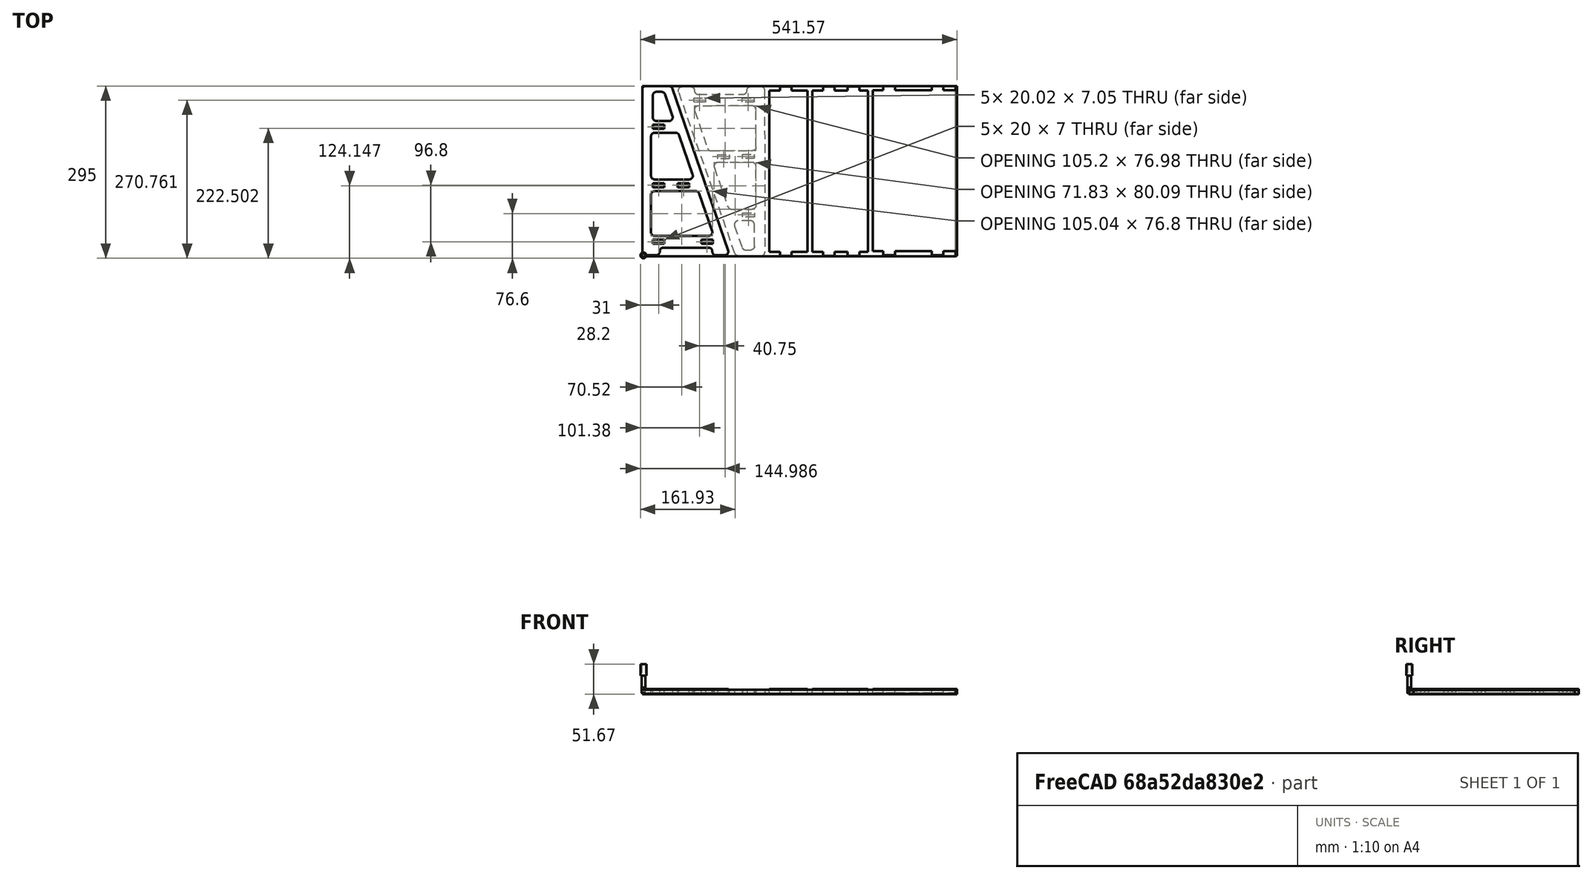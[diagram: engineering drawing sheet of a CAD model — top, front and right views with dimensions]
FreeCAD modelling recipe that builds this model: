
FCSTD DOCUMENT  (FreeCAD 0.20Rpre_28919.fc36 (Git))
Label: Stand5_DB
License: All rights reserved
LicenseURL: http://en.wikipedia.org/wiki/All_rights_reserved
objects: Part::FeaturePython×17, Path::FeaturePython×15, Sketcher::SketchObject×5, PartDesign::Body×5, PartDesign::Pad×4, App::DocumentObjectGroup×4, Mesh::FeaturePython×3, App::FeaturePython×3, App::MeasureDistance×3, Path::FeatureCompoundPython×2, PartDesign::Fillet×1, Spreadsheet::Sheet×1, Part::Mirroring×1, PartDesign::Revolution×1
note: 45 computed .brp shape members not serialized (recipe doc carries the construction recipe); baked Part::Feature solids carry a one-line shape summary decoded from their .brp

FEATURE [Sketcher::SketchObject] Sketch
  FullyConstrained = true
  MapMode = 5
  Support = -> [XY_Plane]
  expr: Constraints[101] = <<Spreadsheet>>.Thickness
  expr: Constraints[102] = <<Spreadsheet>>.TongueSize
  expr: Constraints[103] = <<Spreadsheet>>.TongueToBack
  expr: Constraints[104] = 10 - <<Spreadsheet>>.Thickness / 2
  expr: Constraints[113] = <<Spreadsheet>>.Thickness
  expr: Constraints[114] = <<Spreadsheet>>.TongueSize
  expr: Constraints[115] = <<Spreadsheet>>.TongueGapLower
  expr: Constraints[116] = 10 - <<Spreadsheet>>.Thickness / 2
  expr: Constraints[117] = 10 - <<Spreadsheet>>.Thickness / 2
  expr: Constraints[118] = 120 - <<Spreadsheet>>.Thickness / 2
  expr: Constraints[26] = <<Spreadsheet>>.Height
  expr: Constraints[27] = <<Spreadsheet>>.Top
  expr: Constraints[29] = <<Spreadsheet>>.Bottom
  expr: Constraints[55] = <<Spreadsheet>>.TongueToBack
  expr: Constraints[65] = <<Spreadsheet>>.TongueToBack
  expr: Constraints[66] = <<Spreadsheet>>.TongueSize
  expr: Constraints[67] = <<Spreadsheet>>.Thickness
  expr: Constraints[76] = 10 - <<Spreadsheet>>.Thickness / 2
  expr: Constraints[77] = <<Spreadsheet>>.TongueToBack
  expr: Constraints[78] = <<Spreadsheet>>.Thickness
  expr: Constraints[79] = <<Spreadsheet>>.TongueSize
  expr: Constraints[80] = 10 - <<Spreadsheet>>.Thickness / 2
  expr: Constraints[89] = <<Spreadsheet>>.Thickness
  expr: Constraints[90] = 10 - <<Spreadsheet>>.Thickness / 2
  expr: Constraints[91] = <<Spreadsheet>>.TongueSize
  expr: Constraints[92] = <<Spreadsheet>>.TongueGapMid
  sketch-geometry (40):
    g0: LineSegment StartX=0 StartY=290 StartZ=0 EndX=50 EndY=290 EndZ=0
    g1: LineSegment StartX=150 StartY=0 StartZ=0 EndX=120 EndY=0 EndZ=0
    g2: LineSegment StartX=0 StartY=0 StartZ=0 EndX=0 EndY=290 EndZ=0
    g3: LineSegment StartX=50 StartY=290 StartZ=0 EndX=150 EndY=0 EndZ=0
    g4: LineSegment StartX=15 StartY=210 StartZ=0 EndX=15 EndY=130 EndZ=0
    g5: LineSegment StartX=15 StartY=130 StartZ=0 EndX=89.3057 EndY=130 EndZ=0
    g6: LineSegment StartX=89.3057 StartY=130 StartZ=0 EndX=61.7195 EndY=210 EndZ=0
    g7: LineSegment StartX=61.7195 StartY=210 StartZ=0 EndX=15 EndY=210 EndZ=0
    g8: LineSegment StartX=15 StartY=110 StartZ=0 EndX=15 EndY=33.2 EndZ=0
    g9: LineSegment StartX=15 StartY=33.2 StartZ=0 EndX=122.685 EndY=33.2 EndZ=0
    g10: LineSegment StartX=122.685 StartY=33.2 StartZ=0 EndX=96.2022 EndY=110 EndZ=0
    g11: LineSegment StartX=96.2022 StartY=110 StartZ=0 EndX=15 EndY=110 EndZ=0
    g12: LineSegment StartX=120 StartY=0 StartZ=0 EndX=120 EndY=13.2 EndZ=0
    g13: LineSegment StartX=120 StartY=13.2 StartZ=0 EndX=30 EndY=13.2 EndZ=0
    g14: LineSegment StartX=30 StartY=13.2 StartZ=0 EndX=30 EndY=0 EndZ=0
    g15: LineSegment StartX=30 StartY=0 StartZ=0 EndX=0 EndY=0 EndZ=0
    g16: LineSegment StartX=18 StartY=280 StartZ=0 EndX=18 EndY=230 EndZ=0
    g17: LineSegment StartX=18 StartY=230 StartZ=0 EndX=54.8229 EndY=230 EndZ=0
    g18: LineSegment StartX=54.8229 StartY=230 StartZ=0 EndX=37.5815 EndY=280 EndZ=0
    g19: LineSegment StartX=37.5815 StartY=280 StartZ=0 EndX=18 EndY=280 EndZ=0
    g20: LineSegment StartX=18 StartY=223.5 StartZ=0 EndX=38 EndY=223.5 EndZ=0
    g21: LineSegment StartX=38 StartY=223.5 StartZ=0 EndX=38 EndY=216.5 EndZ=0
    g22: LineSegment StartX=38 StartY=216.5 StartZ=0 EndX=18 EndY=216.5 EndZ=0
    g23: LineSegment StartX=18 StartY=216.5 StartZ=0 EndX=18 EndY=223.5 EndZ=0
    g24: LineSegment StartX=18 StartY=123.5 StartZ=0 EndX=38 EndY=123.5 EndZ=0
    g25: LineSegment StartX=38 StartY=123.5 StartZ=0 EndX=38 EndY=116.5 EndZ=0
    g26: LineSegment StartX=38 StartY=116.5 StartZ=0 EndX=18 EndY=116.5 EndZ=0
    g27: LineSegment StartX=18 StartY=116.5 StartZ=0 EndX=18 EndY=123.5 EndZ=0
    g28: LineSegment StartX=60.5 StartY=123.5 StartZ=0 EndX=80.5 EndY=123.5 EndZ=0
    g29: LineSegment StartX=80.5 StartY=123.5 StartZ=0 EndX=80.5 EndY=116.5 EndZ=0
    g30: LineSegment StartX=80.5 StartY=116.5 StartZ=0 EndX=60.5 EndY=116.5 EndZ=0
    g31: LineSegment StartX=60.5 StartY=116.5 StartZ=0 EndX=60.5 EndY=123.5 EndZ=0
    g32: LineSegment StartX=18 StartY=26.7 StartZ=0 EndX=38 EndY=26.7 EndZ=0
    g33: LineSegment StartX=38 StartY=26.7 StartZ=0 EndX=38 EndY=19.7 EndZ=0
    g34: LineSegment StartX=38 StartY=19.7 StartZ=0 EndX=18 EndY=19.7 EndZ=0
    g35: LineSegment StartX=18 StartY=19.7 StartZ=0 EndX=18 EndY=26.7 EndZ=0
    g36: LineSegment StartX=101 StartY=26.7 StartZ=0 EndX=121 EndY=26.7 EndZ=0
    g37: LineSegment StartX=121 StartY=26.7 StartZ=0 EndX=121 EndY=19.7 EndZ=0
    g38: LineSegment StartX=121 StartY=19.7 StartZ=0 EndX=101 EndY=19.7 EndZ=0
    g39: LineSegment StartX=101 StartY=19.7 StartZ=0 EndX=101 EndY=26.7 EndZ=0
  constraints (119):
    c: Coincident(g15,g2)
    c: Coincident(g2,g0)
    c: Horizontal(g0)
    c: Horizontal(g1)
    c: Vertical(g2)
    c: Vertical(g4)
    c: Coincident(g4,g5)
    c: Horizontal(g5)
    c: Coincident(g5,g6)
    c: Coincident(g6,g7)
    c: Coincident(g7,g4)
    c: Vertical(g8)
    c: Coincident(g8,g9)
    c: Coincident(g9,g10)
    c: Coincident(g10,g11)
    c: Coincident(g11,g8)
    c: Horizontal(g11)
    c: Coincident(g12,g13)
    c: Coincident(g13,g14)
    c: Horizontal(g13)
    c: Vertical(g12)
    c: Vertical(g14)
    c: Coincident(g15,g-1)
    c: Coincident(g0,g3)
    c: Parallel(g3,g10)
    c: Parallel(g3,g6)
    c: DistanceY(g2,g2) = 290
    c: DistanceX(g0,g0) = 50
    c: Coincident(g3,g1)
    c: DistanceX(g2,g1) = 150
    c: DistanceX(g15,g15) = 30
    c: DistanceX(g1,g1) = 30
    c: Coincident(g12,g1)
    c: Parallel(g13,g9)
    c: Parallel(g5,g7)
    c: Coincident(g14,g15)
    c: DistanceY(g14,g13) = 13.2
    c: DistanceY(g13,g8) = 20
    c: DistanceY(g8,g4) = 20
    c: DistanceY(g4,g0) = 80
    c: DistanceX(g2,g8) = 15
    c: DistanceX(g2,g4) = 15
    c: Horizontal(g15)
    c: Distance(g5,g3) = 15
    c: Distance(g10,g3) = 15
    c: DistanceY(g1,g2) = 0
    c: Vertical(g16)
    c: Coincident(g16,g17)
    c: Horizontal(g17)
    c: Coincident(g17,g18)
    c: Coincident(g18,g19)
    c: Coincident(g19,g16)
    c: Horizontal(g19)
    c: DistanceY(g16,g0) = 10
    c: Parallel(g18,g3)
    c: DistanceX(g0,g16) = 18
    c: Distance(g17,g3) = 15
    c: Coincident(g20,g21)
    c: Coincident(g21,g22)
    c: Coincident(g22,g23)
    c: Coincident(g23,g20)
    c: Horizontal(g20)
    c: Horizontal(g22)
    c: Vertical(g21)
    c: Vertical(g23)
    c: DistanceX(g0,g20) = 18
    c: DistanceX(g20,g20) = 20
    c: DistanceY(g23,g23) = 7
    c: Coincident(g24,g25)
    c: Coincident(g25,g26)
    c: Coincident(g26,g27)
    c: Coincident(g27,g24)
    c: Horizontal(g24)
    c: Horizontal(g26)
    c: Vertical(g25)
    c: Vertical(g27)
    c: DistanceY(g20,g16) = 6.5
    c: DistanceX(g2,g26) = 18
    c: DistanceY(g27,g27) = 7
    c: DistanceX(g26,g26) = 20
    c: DistanceY(g24,g4) = 6.5
    c: Coincident(g28,g29)
    c: Coincident(g29,g30)
    c: Coincident(g30,g31)
    c: Coincident(g31,g28)
    c: Horizontal(g28)
    c: Horizontal(g30)
    c: Vertical(g29)
    c: Vertical(g31)
    c: DistanceY(g31,g31) = 7
    c: DistanceY(g28,g5) = 6.5
    c: DistanceX(g30,g30) = 20
    c: DistanceX(g24,g28) = 22.5
    c: Coincident(g32,g33)
    c: Coincident(g33,g34)
    c: Coincident(g34,g35)
    c: Coincident(g35,g32)
    c: Horizontal(g32)
    c: Horizontal(g34)
    c: Vertical(g33)
    c: Vertical(g35)
    c: DistanceY(g35,g35) = 7
    c: DistanceX(g32,g32) = 20
    c: DistanceX(g2,g34) = 18
    c: DistanceY(g32,g8) = 6.5
    c: Coincident(g36,g37)
    c: Coincident(g37,g38)
    c: Coincident(g38,g39)
    c: Coincident(g39,g36)
    c: Horizontal(g36)
    c: Horizontal(g38)
    c: Vertical(g37)
    c: Vertical(g39)
    c: DistanceY(g39,g39) = 7
    c: DistanceX(g36,g36) = 20
    c: DistanceX(g32,g36) = 63
    c: DistanceY(g36,g9) = 6.5
    c: DistanceY(g4,g22) = 6.5
    c: DistanceY(g2,g26) = 116.5
FEATURE [PartDesign::Pad] Pad
  Direction = (0,0,1)
  Length = 7
  Length2 = 100
  Profile = -> Sketch
  Type = 0
  expr: Length = <<Spreadsheet>>.Thickness
FEATURE [PartDesign::Fillet] Fillet
  Base = -> Pad [Edge20,Edge2,Edge1,Edge5,Edge8,Edge17,Edge44,Edge37,Edge32,Edge25,Edge38,Edge26,Edge29,Edge41,Edge14,Edge11,Edge49,Edge50,Edge56,Edge53]
  BaseFeature = -> Pad
  Radius = 6.5
  SupportTransform = false
  UseAllEdges = false
  expr: Radius = <<Spreadsheet>>.Tool
FEATURE [PartDesign::Body] Body
  Group = -> [Sketch,Pad,Fillet]
  Origin = -> Origin
  Placement = pos=(-2,0,0) rot=(0,0,1;0rad)
  Tip = -> Fillet
FEATURE [Spreadsheet::Sheet] Spreadsheet
  cells = A2=Material Thickness; B2(Thickness)=7; A3=Tool Size; B3(Tool)=6.5; A5=Height; B5(Height)=290; A6=Bottom Width; B6(Bottom)=150; A7=Top Width; B7(Top)=50; A8=SlotSize; B8(SlotSize)=20; A9=TongueSize; B9(TongueSize)==B8; A10=Tongue to back; B10(TongueToBack)=18; A11=Centre; B11(SlotCentre)=120; A12=Mid Tongue Gap; B12(TongueGapMid)=22.5; A13=Lower Tongue Gap; B13(TongueGapLower)=63; A15=TopShelf; B15(ShelfTop)=65; A16=MidShelf; B16(ShelfMid)==(B6 + B7) / 2 - 5; A17=Bottom Shelf; B17(ShelfBottom)==B6 - 6; A18=Shelf Width; B18(ShelfWidth)==B5 - B2 * 2
FEATURE [Part::Mirroring] mirror  label="Body (mirrored) "
  Base = (159.181,124.226,5.79083)
  Normal = (-0.999887,-0.00161748,0.0149187)
  Placement = pos=(-113.202,287.893,10.586) rot=(0.99989,0.002927,-0.014571;3.14394rad)
  Source = -> Body
FEATURE [Sketcher::SketchObject] Sketch001
  FullyConstrained = false
  MapMode = 5
  Support = -> [XY_Plane001]
  expr: Constraints[15] = <<Spreadsheet>>.TongueSize
  expr: Constraints[16] = <<Spreadsheet>>.Thickness
  expr: Constraints[24] = <<Spreadsheet>>.TongueSize
  expr: Constraints[25] = <<Spreadsheet>>.Thickness
  expr: Constraints[26] = <<Spreadsheet>>.TongueToBack
  expr: Constraints[27] = <<Spreadsheet>>.TongueToBack
  expr: Constraints[31] = <<Spreadsheet>>.ShelfWidth
  expr: Constraints[8] = <<Spreadsheet>>.ShelfTop
  expr: Constraints[9] = <<Spreadsheet>>.ShelfWidth
  sketch-geometry (12):
    g0: LineSegment StartX=222.605 StartY=283 StartZ=0 EndX=240.605 EndY=283 EndZ=0
    g1: LineSegment StartX=287.605 StartY=283 StartZ=0 EndX=287.605 EndY=7 EndZ=0
    g2: LineSegment StartX=287.605 StartY=7 StartZ=0 EndX=260.605 EndY=7 EndZ=0
    g3: LineSegment StartX=222.605 StartY=7 StartZ=0 EndX=222.605 EndY=283 EndZ=0
    g4: LineSegment StartX=260.605 StartY=7 StartZ=0 EndX=260.605 EndY=0 EndZ=0
    g5: LineSegment StartX=260.605 StartY=0 StartZ=0 EndX=240.605 EndY=0 EndZ=0
    g6: LineSegment StartX=240.605 StartY=0 StartZ=0 EndX=240.605 EndY=7 EndZ=0
    g7: LineSegment StartX=240.605 StartY=7 StartZ=0 EndX=222.605 EndY=7 EndZ=0
    g8: LineSegment StartX=240.605 StartY=290 StartZ=0 EndX=260.605 EndY=290 EndZ=0
    g9: LineSegment StartX=260.605 StartY=290 StartZ=0 EndX=260.605 EndY=283 EndZ=0
    g10: LineSegment StartX=240.605 StartY=283 StartZ=0 EndX=240.605 EndY=290 EndZ=0
    g11: LineSegment StartX=260.605 StartY=283 StartZ=0 EndX=287.605 EndY=283 EndZ=0
  constraints (35):
    c: Coincident(g11,g1)
    c: Coincident(g1,g2)
    c: Coincident(g7,g3)
    c: Coincident(g3,g0)
    c: Horizontal(g0)
    c: Horizontal(g2)
    c: Vertical(g1)
    c: Vertical(g3)
    c: DistanceX(g0,g11) = 65
    c: DistanceY(g3,g3) = 276
    c: Coincident(g4,g5)
    c: Coincident(g5,g6)
    c: Horizontal(g5)
    c: Vertical(g4)
    c: Vertical(g6)
    c: DistanceX(g5,g5) = 20
    c: DistanceY(g4,g4) = 7
    c: DistanceY(g-1,g5) = 0
    c: Parallel(g5,g7)
    c: Coincident(g8,g9)
    c: Coincident(g10,g8)
    c: Horizontal(g8)
    c: Vertical(g9)
    c: Vertical(g10)
    c: DistanceX(g8,g8) = 20
    c: DistanceY(g9,g9) = 7
    c: DistanceX(g0,g8) = 18
    c: DistanceX(g3,g5) = 18
    c: Coincident(g7,g6)
    c: Coincident(g11,g9)
    c: Coincident(g2,g4)
    c: DistanceY(g1,g1) = 276
    c: Parallel(g11,g8)
    c: Equal(g4,g6)
    c: Coincident(g0,g10)
FEATURE [PartDesign::Pad] Pad001
  Direction = (0,0,1)
  Length = 7
  Length2 = 10
  Profile = -> Sketch001
  Type = 0
  expr: Length = <<Spreadsheet>>.Thickness
FEATURE [PartDesign::Body] Body001  label="TopShelf"
  Group = -> [Sketch001,Pad001]
  Origin = -> Origin001
  Placement = pos=(-7,-1,0) rot=(0,0,1;0rad)
  Tip = -> Pad001
FEATURE [Sketcher::SketchObject] Sketch002
  FullyConstrained = false
  MapMode = 5
  Support = -> [XY_Plane002]
  expr: Constraints[31] = <<Spreadsheet>>.TongueToBack
  expr: Constraints[32] = <<Spreadsheet>>.TongueGapMid
  expr: Constraints[33] = <<Spreadsheet>>.TongueSize
  expr: Constraints[36] = <<Spreadsheet>>.TongueSize
  expr: Constraints[37] = <<Spreadsheet>>.TongueToBack
  expr: Constraints[38] = <<Spreadsheet>>.TongueSize
  expr: Constraints[42] = <<Spreadsheet>>.TongueGapMid
  expr: Constraints[43] = <<Spreadsheet>>.TongueSize
  expr: Constraints[46] = <<Spreadsheet>>.Thickness
  expr: Constraints[47] = <<Spreadsheet>>.Thickness
  expr: Constraints[48] = <<Spreadsheet>>.Thickness
  expr: Constraints[49] = <<Spreadsheet>>.Thickness
  expr: Constraints[54] = <<Spreadsheet>>.Thickness
  expr: Constraints[55] = <<Spreadsheet>>.Thickness
  expr: Constraints[56] = <<Spreadsheet>>.Thickness
  expr: Constraints[57] = <<Spreadsheet>>.ShelfWidth
  expr: Constraints[58] = <<Spreadsheet>>.Thickness
  expr: Constraints[8] = <<Spreadsheet>>.ShelfWidth
  expr: Constraints[9] = <<Spreadsheet>>.ShelfMid
  sketch-geometry (20):
    g0: LineSegment StartX=282.276 StartY=276 StartZ=0 EndX=300.276 EndY=276 EndZ=0
    g1: LineSegment StartX=377.276 StartY=276 StartZ=0 EndX=377.276 EndY=0 EndZ=0
    g2: LineSegment StartX=377.276 StartY=0 StartZ=0 EndX=362.776 EndY=0 EndZ=0
    g3: LineSegment StartX=282.276 StartY=0 StartZ=0 EndX=282.276 EndY=276 EndZ=0
    g4: LineSegment StartX=300.276 StartY=283 StartZ=0 EndX=320.276 EndY=283 EndZ=0
    g5: LineSegment StartX=320.276 StartY=283 StartZ=0 EndX=320.276 EndY=276 EndZ=0
    g6: LineSegment StartX=300.276 StartY=276 StartZ=0 EndX=300.276 EndY=283 EndZ=0
    g7: LineSegment StartX=342.776 StartY=283 StartZ=0 EndX=362.776 EndY=283 EndZ=0
    g8: LineSegment StartX=362.776 StartY=283 StartZ=0 EndX=362.776 EndY=276 EndZ=0
    g9: LineSegment StartX=342.776 StartY=276 StartZ=0 EndX=342.776 EndY=283 EndZ=0
    g10: LineSegment StartX=320.276 StartY=-2e-16 StartZ=0 EndX=320.276 EndY=-7 EndZ=0
    g11: LineSegment StartX=320.276 StartY=-7 StartZ=0 EndX=300.276 EndY=-7 EndZ=0
    g12: LineSegment StartX=300.276 StartY=-7 StartZ=0 EndX=300.276 EndY=0 EndZ=0
    g13: LineSegment StartX=362.776 StartY=0 StartZ=0 EndX=362.776 EndY=-7 EndZ=0
    g14: LineSegment StartX=362.776 StartY=-7 StartZ=0 EndX=342.776 EndY=-7 EndZ=0
    g15: LineSegment StartX=342.776 StartY=-7 StartZ=0 EndX=342.776 EndY=0 EndZ=0
    g16: LineSegment StartX=320.276 StartY=276 StartZ=0 EndX=342.776 EndY=276 EndZ=0
    g17: LineSegment StartX=362.776 StartY=276 StartZ=0 EndX=377.276 EndY=276 EndZ=0
    g18: LineSegment StartX=300.276 StartY=0 StartZ=0 EndX=282.276 EndY=0 EndZ=0
    g19: LineSegment StartX=342.776 StartY=0 StartZ=0 EndX=320.276 EndY=-2e-16 EndZ=0
  constraints (60):
    c: Coincident(g17,g1)
    c: Coincident(g1,g2)
    c: Coincident(g18,g3)
    c: Coincident(g3,g0)
    c: Horizontal(g0)
    c: Horizontal(g2)
    c: Vertical(g1)
    c: Vertical(g3)
    c: DistanceY(g1,g1) = 276
    c: DistanceX(g0,g17) = 95
    c: Coincident(g4,g5)
    c: Coincident(g6,g4)
    c: Horizontal(g4)
    c: Vertical(g5)
    c: Vertical(g6)
    c: Coincident(g7,g8)
    c: Coincident(g9,g7)
    c: Horizontal(g7)
    c: Vertical(g8)
    c: Vertical(g9)
    c: PointOnObject(g8,g0)
    c: Coincident(g10,g11)
    c: Coincident(g11,g12)
    c: Horizontal(g11)
    c: Vertical(g10)
    c: Vertical(g12)
    c: Coincident(g13,g14)
    c: Coincident(g14,g15)
    c: Horizontal(g14)
    c: Vertical(g13)
    c: Vertical(g15)
    c: DistanceX(g0,g4) = 18
    c: DistanceX(g4,g7) = 22.5
    c: DistanceX(g4,g4) = 20
    c: Coincident(g16,g5)
    c: PointOnObject(g16,g9)
    c: DistanceX(g7,g7) = 20
    c: DistanceX(g3,g11) = 18
    c: DistanceX(g11,g11) = 20
    c: Coincident(g18,g12)
    c: Coincident(g10,g19)
    c: Coincident(g19,g15)
    c: DistanceX(g19,g19) = 22.5
    c: DistanceX(g14,g14) = 20
    c: Coincident(g0,g6)
    c: Coincident(g17,g8)
    c: DistanceY(g1,g7) = 7
    c: DistanceY(g9,g9) = 7
    c: DistanceY(g5,g5) = 7
    c: DistanceY(g6,g6) = 7
    c: Parallel(g16,g4)
    c: Parallel(g18,g11)
    c: Parallel(g19,g11)
    c: Coincident(g2,g13)
    c: DistanceY(g12,g12) = 7
    c: DistanceY(g15,g15) = 7
    c: DistanceY(g13,g13) = 7
    c: DistanceY(g3,g3) = 276
    c: DistanceY(g10,g10) = 7
    c: PointOnObject(g3,g-1)
FEATURE [PartDesign::Pad] Pad002
  Direction = (0,0,1)
  Length = 7
  Length2 = 10
  Profile = -> Sketch002
  Type = 0
  expr: Length = <<Spreadsheet>>.Thickness
FEATURE [PartDesign::Body] Body002  label="MidShelf"
  Group = -> [Sketch002,Pad002]
  Origin = -> Origin002
  Placement = pos=(7,6,0) rot=(0,0,1;0rad)
  Tip = -> Pad002
FEATURE [Sketcher::SketchObject] Sketch003
  FullyConstrained = false
  MapMode = 5
  Support = -> [XY_Plane003]
  expr: Constraints[34] = <<Spreadsheet>>.TongueSize
  expr: Constraints[35] = <<Spreadsheet>>.TongueSize
  expr: Constraints[36] = <<Spreadsheet>>.TongueGapLower
  expr: Constraints[37] = <<Spreadsheet>>.TongueToBack
  expr: Constraints[44] = <<Spreadsheet>>.Thickness
  expr: Constraints[45] = <<Spreadsheet>>.Thickness
  expr: Constraints[46] = <<Spreadsheet>>.Thickness
  expr: Constraints[48] = <<Spreadsheet>>.ShelfWidth
  expr: Constraints[49] = <<Spreadsheet>>.Thickness
  expr: Constraints[4] = <<Spreadsheet>>.ShelfBottom
  expr: Constraints[50] = <<Spreadsheet>>.Thickness
  expr: Constraints[51] = <<Spreadsheet>>.TongueSize
  expr: Constraints[52] = <<Spreadsheet>>.TongueSize
  expr: Constraints[53] = <<Spreadsheet>>.TongueGapLower
  expr: Constraints[54] = <<Spreadsheet>>.TongueToBack
  expr: Constraints[55] = <<Spreadsheet>>.ShelfWidth
  expr: Constraints[56] = <<Spreadsheet>>.Thickness
  expr: Constraints[57] = <<Spreadsheet>>.Thickness
  expr: Constraints[58] = 11mm
  sketch-geometry (20):
    g0: LineSegment StartX=535.567 StartY=287 StartZ=0 EndX=535.567 EndY=11 EndZ=0
    g1: LineSegment StartX=535.567 StartY=11 StartZ=0 EndX=512.567 EndY=11 EndZ=0
    g2: LineSegment StartX=391.567 StartY=11 StartZ=0 EndX=391.567 EndY=287 EndZ=0
    g3: LineSegment StartX=409.567 StartY=294 StartZ=0 EndX=429.567 EndY=294 EndZ=0
    g4: LineSegment StartX=429.567 StartY=294 StartZ=0 EndX=429.567 EndY=287 EndZ=0
    g5: LineSegment StartX=409.567 StartY=287 StartZ=0 EndX=409.567 EndY=294 EndZ=0
    g6: LineSegment StartX=492.567 StartY=294 StartZ=0 EndX=512.567 EndY=294 EndZ=0
    g7: LineSegment StartX=512.567 StartY=294 StartZ=0 EndX=512.567 EndY=287 EndZ=0
    g8: LineSegment StartX=492.567 StartY=287 StartZ=0 EndX=492.567 EndY=294 EndZ=0
    g9: LineSegment StartX=429.567 StartY=11 StartZ=0 EndX=429.567 EndY=4 EndZ=0
    g10: LineSegment StartX=429.567 StartY=4 StartZ=0 EndX=409.567 EndY=4 EndZ=0
    g11: LineSegment StartX=409.567 StartY=4 StartZ=0 EndX=409.567 EndY=11 EndZ=0
    g12: LineSegment StartX=512.567 StartY=11 StartZ=0 EndX=512.567 EndY=4 EndZ=0
    g13: LineSegment StartX=512.567 StartY=4 StartZ=0 EndX=492.567 EndY=4 EndZ=0
    g14: LineSegment StartX=492.567 StartY=4 StartZ=0 EndX=492.567 EndY=11 EndZ=0
    g15: LineSegment StartX=391.567 StartY=287 StartZ=0 EndX=409.567 EndY=287 EndZ=0
    g16: LineSegment StartX=429.567 StartY=287 StartZ=0 EndX=492.567 EndY=287 EndZ=0
    g17: LineSegment StartX=512.567 StartY=287 StartZ=0 EndX=535.567 EndY=287 EndZ=0
    g18: LineSegment StartX=409.567 StartY=11 StartZ=0 EndX=391.567 EndY=11 EndZ=0
    g19: LineSegment StartX=492.567 StartY=11 StartZ=0 EndX=429.567 EndY=11 EndZ=0
  constraints (59):
    c: Coincident(g0,g1)
    c: Coincident(g18,g2)
    c: Horizontal(g1)
    c: Vertical(g0)
    c: DistanceX(g2,g0) = 144
    c: Coincident(g3,g4)
    c: Coincident(g5,g3)
    c: Horizontal(g3)
    c: Vertical(g4)
    c: Vertical(g5)
    c: Coincident(g6,g7)
    c: Coincident(g8,g6)
    c: Horizontal(g6)
    c: Vertical(g7)
    c: Vertical(g8)
    c: Coincident(g9,g10)
    c: Coincident(g10,g11)
    c: Horizontal(g10)
    c: Vertical(g9)
    c: Vertical(g11)
    c: Coincident(g12,g13)
    c: Coincident(g13,g14)
    c: Horizontal(g13)
    c: Vertical(g12)
    c: Vertical(g14)
    c: Horizontal(g17)
    c: Coincident(g7,g17)
    c: Coincident(g17,g0)
    c: Coincident(g8,g16)
    c: Coincident(g16,g4)
    c: Coincident(g15,g5)
    c: Coincident(g2,g15)
    c: Parallel(g15,g3)
    c: Parallel(g16,g3)
    c: DistanceX(g3,g3) = 20
    c: DistanceX(g6,g6) = 20
    c: DistanceX(g3,g6) = 63
    c: DistanceX(g2,g3) = 18
    c: Coincident(g18,g11)
    c: Coincident(g9,g19)
    c: Coincident(g19,g14)
    c: Coincident(g12,g1)
    c: Parallel(g18,g10)
    c: Parallel(g10,g19)
    c: DistanceY(g11,g11) = 7
    c: DistanceY(g9,g9) = 7
    c: DistanceY(g14,g14) = 7
    c: Perpendicular(g18,g2)
    c: DistanceY(g2,g2) = 276
    c: DistanceY(g5,g5) = 7
    c: DistanceY(g8,g8) = 7
    c: DistanceX(g10,g10) = 20
    c: DistanceX(g13,g13) = 20
    c: DistanceX(g19,g19) = 63
    c: DistanceX(g18,g18) = 18
    c: DistanceY(g0,g0) = 276
    c: DistanceY(g12,g12) = 7
    c: DistanceY(g7,g7) = 7
    c: DistanceY(g-1,g2) = 11
FEATURE [PartDesign::Pad] Pad003
  Direction = (0,0,1)
  Length = 7
  Length2 = 10
  Profile = -> Sketch003
  Type = 0
  expr: Length = <<Spreadsheet>>.Thickness
FEATURE [PartDesign::Body] Body003  label="BottomShelf"
  Group = -> [Sketch003,Pad003]
  Origin = -> Origin003
  Placement = pos=(1,-4,0) rot=(0,0,1;0rad)
  Tip = -> Pad003
FEATURE [Mesh::FeaturePython] CutMaterial001  # WARN: FeaturePython — macro-defined, semantics opaque (R4)
FEATURE [App::FeaturePython] SetupSheet  # Path/CAM operation (typed FeaturePython)
  ClearanceHeightExpression = OpStockZMax+SetupSheet.ClearanceHeightOffset
  ClearanceHeightOffset = 5
  CoolantMode = 0
  CoolantModes = None | Flood | Mist
  FinalDepthExpression = OpFinalDepth
  HorizRapid = 0
  SafeHeightExpression = OpStockZMax+SetupSheet.SafeHeightOffset
  SafeHeightOffset = 3
  StartDepthExpression = OpStartDepth
  StepDownExpression = OpToolDiameter
  VertRapid = 0
FEATURE [Part::FeaturePython] Clone  label="Model-Body"  # Draft clone (typed FeaturePython)
  AttacherType = Attacher::AttachEngine3D
  Fuse = false
  Objects = -> [Body]
  PathResource = Model
  Placement = pos=(-2,0,0) rot=(0,0,1;0rad)
  Scale = (1,1,1)
FEATURE [Part::FeaturePython] Clone001  label="Model-Body (mirrored) "  # Draft clone (typed FeaturePython)
  AttacherType = Attacher::AttachEngine3D
  Fuse = false
  Objects = -> [mirror]
  PathResource = Model
  Placement = pos=(-113.202,287.893,10.586) rot=(0.99989,0.002927,-0.014571;3.14394rad)
  Scale = (1,1,1)
FEATURE [Part::FeaturePython] Clone002  label="Model-BottomShelf"  # Draft clone (typed FeaturePython)
  AttacherType = Attacher::AttachEngine3D
  Fuse = false
  Objects = -> [Body003]
  PathResource = Model
  Placement = pos=(1,-4,0) rot=(0,0,1;0rad)
  Scale = (1,1,1)
FEATURE [Part::FeaturePython] Clone003  label="Model-MidShelf"  # Draft clone (typed FeaturePython)
  AttacherType = Attacher::AttachEngine3D
  Fuse = false
  Objects = -> [Body002]
  PathResource = Model
  Placement = pos=(7,6,0) rot=(0,0,1;0rad)
  Scale = (1,1,1)
FEATURE [Part::FeaturePython] Clone004  label="Model-TopShelf"  # Draft clone (typed FeaturePython)
  AttacherType = Attacher::AttachEngine3D
  Fuse = false
  Objects = -> [Body001]
  PathResource = Model
  Placement = pos=(-7,-1,0) rot=(0,0,1;0rad)
  Scale = (1,1,1)
FEATURE [App::DocumentObjectGroup] Model
  Group = -> [Clone,Clone001,Clone002,Clone003,Clone004,SetupSheet]
FEATURE [Part::FeaturePython] Stock001  # WARN: FeaturePython — macro-defined, semantics opaque (R4)
  Height = 7.17
  Length = 536.13
  Placement = pos=(-2,-1.61323,-0.917831) rot=(0,0,1;0rad)
  StockType = CreateBox
  Width = 291.61
FEATURE [Part::FeaturePython] ToolBit001  label="6.4mm Endmill"  # Path/CAM toolbit (typed FeaturePython)
  BitPropertyNames = Chipload | CuttingEdgeHeight | Diameter | Flutes | Length | Material | ShankDiameter
  BitShape = <path>
  Chipload = 0
  CuttingEdgeHeight = 30
  Diameter = 6.4
  File = <userpath>/MensShed/CNCRouter/FreeCAD/Bit/6.4mm_Endmill.fctb
  Flutes = 0
  Length = 50
  Material = 0
  ShankDiameter = 10
  ShapeName = endmill
FEATURE [Sketcher::SketchObject] Sketch004
  FullyConstrained = true
  MapMode = 5
  Placement = pos=(0,0,0) rot=(1,0,0;1.5708rad)
  Support = -> [XZ_Plane004]
  expr: Constraints[10] = <<Attributes>>.Length
  expr: Constraints[16] = <<Attributes>>.ShankDiameter
  expr: Constraints[18] = <<Attributes>>.CuttingEdgeHeight
  expr: Constraints[9] = <<Attributes>>.Diameter
  sketch-geometry (8):
    g0: LineSegment StartX=0 StartY=50 StartZ=0 EndX=0 EndY=0 EndZ=0
    g1: LineSegment StartX=0 StartY=0 StartZ=0 EndX=3.2 EndY=0 EndZ=0
    g2: LineSegment StartX=3.2 StartY=0 StartZ=0 EndX=3.2 EndY=30 EndZ=0
    g3: LineSegment StartX=5 StartY=50 StartZ=0 EndX=0 EndY=50 EndZ=0
    g4: LineSegment StartX=3.2 StartY=0 StartZ=0 EndX=-3.2 EndY=0 EndZ=0
    g5: LineSegment StartX=5 StartY=29.99 StartZ=0 EndX=3.2 EndY=30 EndZ=0
    g6: LineSegment StartX=5 StartY=50 StartZ=0 EndX=5 EndY=29.99 EndZ=0
    g7: LineSegment StartX=-5 StartY=50 StartZ=0 EndX=5 EndY=50 EndZ=0
  constraints (21):
    c: Vertical(g0)
    c: Coincident(g0,g1)
    c: Horizontal(g1)
    c: Coincident(g1,g2)
    c: Vertical(g2)
    c: Horizontal(g3)
    c: Coincident(g0,g3)
    c: Coincident(g4,g1)
    c: Symmetric(g1,g4,g0)
    c: DistanceX(g4,g4) = 6.4
    c: DistanceY(g2,g3) = 50
    c: Coincident(g2,g5)
    c: Vertical(g6)
    c: Coincident(g3,g6)
    c: Symmetric(g7,g7,g0)
    c: Coincident(g7,g3)
    c: DistanceX(g7,g7) = 10
    c: Coincident(g5,g6)
    c: DistanceY(g2) = 30
    c: Coincident(g0,g-1)
    c: DistanceY(g5,g2) = 0.01
FEATURE [PartDesign::Revolution] Revolution
  AllowMultiFace = false
  Angle = 360
  Axis = (0,-2e-16,1)
  Base = (0,0,0)
  Placement = pos=(0,0,0) rot=(1,0,0;1.5708rad)
  Profile = -> Sketch004
  ReferenceAxis = -> Sketch004 [V_Axis]
  Reversed = true
FEATURE [App::FeaturePython] PropertyBag  label="Attributes"  # WARN: FeaturePython — macro-defined, semantics opaque (R4)
  Chipload = 0
  CustomPropertyGroups = Attributes | Shape
  CuttingEdgeHeight = 30
  Diameter = 6.4
  Flutes = 0
  Length = 50
  Material = 0
  ShankDiameter = 10
FEATURE [PartDesign::Body] Body004  label="Endmill001"
  Group = -> [Sketch004,Revolution,PropertyBag]
  Origin = -> Origin004
  Tip = -> Revolution
FEATURE [Part::FeaturePython] ToolBit  label="6.4mm Endmill002"  # Path/CAM toolbit (typed FeaturePython)
  BitBody = -> Body004
  BitPropertyNames = Chipload | CuttingEdgeHeight | Diameter | Flutes | Length | Material | ShankDiameter
  BitShape = <path>
  Chipload = 0
  CuttingEdgeHeight = 30
  Diameter = 6.4
  Flutes = 0
  Length = 50
  Material = 0
  ShankDiameter = 10
  ShapeName = endmill
FEATURE [Part::FeaturePython] ToolBit002  label="6.4mm Endmill003"  # Path/CAM toolbit (typed FeaturePython)
  BitPropertyNames = Chipload | CuttingEdgeHeight | Diameter | Flutes | Length | Material | ShankDiameter
  BitShape = <path>
  Chipload = 0
  CuttingEdgeHeight = 30
  Diameter = 6.4
  Flutes = 0
  Length = 50
  Material = 0
  ShankDiameter = 10
  ShapeName = endmill
FEATURE [Path::FeaturePython] __4mm_Endmill  label="6.4mm Endmill001"  # Path/CAM operation (typed FeaturePython)
  HorizFeed = 13.5167
  HorizRapid = 0
  SpindleDir = 1
  SpindleSpeed = 12682
  Tool = -> ToolBit002
  ToolNumber = 2
  VertFeed = 6.75
  VertRapid = 0
  expr: VertRapid = SetupSheet.VertRapid
FEATURE [Path::FeaturePython] Profile  label="BaseInner"  # Path/CAM operation (typed FeaturePython)
  Active = true
  AreaParams:
    Tolerance = 1e-07
    FitArcs = True
    Simplify = False
    CleanDistance = 0.0
    Accuracy = 0.01
    Unit = 1.0
    MinArcPoints = 4
    MaxArcPoints = 100
    ClipperScale = 10000000.0
    Fill = 0
    Coplanar = 0
    Reorient = True
    Outline = False
    Explode = False
    OpenMode = 0
    Deflection = 0.01
    SubjectFill = 0
    ClipFill = 0
    Offset = -3.2
    ExtraPass = 0
    Stepover = 0.0
    LastStepover = 0.0
    JoinType = 0
    EndType = 0
    MiterLimit = 2.0
    RoundPrecision = 0.0
    PocketMode = 0
    ToolRadius = 1.0
    PocketExtraOffset = 0.0
    PocketStepover = 0.0
    PocketLastStepover = 0.0
    FromCenter = False
    Angle = 45.0
    AngleShift = 0.0
    Shift = 0.0
    Thicken = False
    SectionCount = -1
    Stepdown = 1.0
    SectionOffset = 0.0
    SectionTolerance = 1e-06
    SectionMode = 2
    Project = False
  AttemptInverseAngle = true
  Base = -> [Clone]
  ClearanceHeight = 11.2522
  CoolantMode = 0
  CycleTime = 00:03:00
  Direction = 0
  EnableRotation = 0
  FinalDepth = 0.2
  HandleMultipleFeatures = 0
  InverseAngle = false
  JoinType = 0
  LimitDepthToFace = true
  MiterLimit = 0.1
  OffsetExtra = 0
  OpFinalDepth = 7
  OpStartDepth = 10
  OpStockZMax = 6.25217
  OpStockZMin = -0.917831
  OpToolDiameter = 6.4
  PathParams = {'orientation': 1, 'feedrate': 13.516666666666666, 'feedrate_v': 6.75, 'verbose': True, 'resume_height': 9.252168804445907, 'retraction': 11.252168804445907, 'return_end': True, 'preamble': False, 'start': Vector (79.51085861020287, 133.4790016587114, 11.252168804445907)}
  ReverseDirection = false
  SafeHeight = 9.25217
  Side = 1
  SplitArcs = false
  StartDepth = 7
  StartPoint = (0,0,0)
  StepDown = 3
  ToolController = -> __4mm_Endmill
  UseComp = true
  UseStartPoint = false
  processCircles = false
  processHoles = false
  processPerimeter = true
  expr: ClearanceHeight = OpStockZMax + SetupSheet.ClearanceHeightOffset
  expr: FinalDepth = 0.2
  expr: SafeHeight = OpStockZMax + SetupSheet.SafeHeightOffset
  expr: StartDepth = <<Spreadsheet>>.Thickness
  expr: StepDown = 3
FEATURE [Path::FeaturePython] Profile001  label="MirrorInner"  # Path/CAM operation (typed FeaturePython)
  Active = true
  AreaParams:
    Tolerance = 1e-07
    FitArcs = True
    Simplify = False
    CleanDistance = 0.0
    Accuracy = 0.01
    Unit = 1.0
    MinArcPoints = 4
    MaxArcPoints = 100
    ClipperScale = 10000000.0
    Fill = 0
    Coplanar = 0
    Reorient = True
    Outline = False
    Explode = False
    OpenMode = 0
    Deflection = 0.01
    SubjectFill = 0
    ClipFill = 0
    Offset = -3.2
    ExtraPass = 0
    Stepover = 0.0
    LastStepover = 0.0
    JoinType = 0
    EndType = 0
    MiterLimit = 2.0
    RoundPrecision = 0.0
    PocketMode = 0
    ToolRadius = 1.0
    PocketExtraOffset = 0.0
    PocketStepover = 0.0
    PocketLastStepover = 0.0
    FromCenter = False
    Angle = 45.0
    AngleShift = 0.0
    Shift = 0.0
    Thicken = False
    SectionCount = -1
    Stepdown = 1.0
    SectionOffset = 0.0
    SectionTolerance = 1e-06
    SectionMode = 2
    Project = False
  AttemptInverseAngle = true
  Base = -> [Clone001]
  ClearanceHeight = 11.2522
  CoolantMode = 0
  CycleTime = 00:03:02
  Direction = 0
  EnableRotation = 0
  FinalDepth = 0.2
  HandleMultipleFeatures = 0
  InverseAngle = false
  JoinType = 0
  LimitDepthToFace = true
  MiterLimit = 0.1
  OffsetExtra = 0
  OpFinalDepth = 5.95233
  OpStartDepth = 6.25217
  OpStockZMax = 6.25217
  OpStockZMin = -0.917831
  OpToolDiameter = 6.4
  PathParams = {'orientation': 1, 'feedrate': 13.516666666666666, 'feedrate_v': 6.75, 'verbose': True, 'resume_height': 9.252168804445907, 'retraction': 11.252168804445907, 'return_end': True, 'preamble': False, 'start': Vector (185.594594529693, 82.4083677149265, 11.252168804445907)}
  ReverseDirection = false
  SafeHeight = 9.25217
  Side = 1
  SplitArcs = false
  StartDepth = 7
  StartPoint = (0,0,0)
  StepDown = 3
  ToolController = -> __4mm_Endmill
  UseComp = true
  UseStartPoint = false
  processCircles = false
  processHoles = false
  processPerimeter = true
  expr: ClearanceHeight = OpStockZMax + SetupSheet.ClearanceHeightOffset
  expr: FinalDepth = 0.2
  expr: SafeHeight = OpStockZMax + SetupSheet.SafeHeightOffset
  expr: StartDepth = <<Spreadsheet>>.Thickness
  expr: StepDown = 3
FEATURE [Path::FeaturePython] Profile002  label="Outer Profile"  # Path/CAM operation (typed FeaturePython)
  Active = true
  AreaParams:
    Tolerance = 1e-07
    FitArcs = True
    Simplify = False
    CleanDistance = 0.0
    Accuracy = 0.01
    Unit = 1.0
    MinArcPoints = 4
    MaxArcPoints = 100
    ClipperScale = 10000000.0
    Fill = 0
    Coplanar = 0
    Reorient = True
    Outline = False
    Explode = False
    OpenMode = 0
    Deflection = 0.01
    SubjectFill = 0
    ClipFill = 0
    Offset = 3.2
    ExtraPass = 0
    Stepover = 0.0
    LastStepover = 0.0
    JoinType = 0
    EndType = 0
    MiterLimit = 2.0
    RoundPrecision = 0.0
    PocketMode = 0
    ToolRadius = 1.0
    PocketExtraOffset = 0.0
    PocketStepover = 0.0
    PocketLastStepover = 0.0
    FromCenter = False
    Angle = 45.0
    AngleShift = 0.0
    Shift = 0.0
    Thicken = False
    SectionCount = -1
    Stepdown = 1.0
    SectionOffset = 0.0
    SectionTolerance = 1e-06
    SectionMode = 2
    Project = False
  AttemptInverseAngle = true
  ClearanceHeight = 11.2522
  CoolantMode = 0
  CycleTime = 00:15:35
  Direction = 0
  EnableRotation = 0
  FinalDepth = 0.2
  HandleMultipleFeatures = 0
  InverseAngle = false
  JoinType = 0
  LimitDepthToFace = true
  MiterLimit = 0.1
  OffsetExtra = 0
  OpFinalDepth = -0.917831
  OpStartDepth = 6.25217
  OpStockZMax = 6.25217
  OpStockZMin = -0.917831
  OpToolDiameter = 6.4
  PathParams = {'orientation': 1, 'feedrate': 13.516666666666666, 'feedrate_v': 6.75, 'verbose': True, 'resume_height': 9.252168804445907, 'retraction': 11.252168804445907, 'return_end': True, 'preamble': False, 'start': Vector (286.075665, 263.59583288242766, 11.252168804445907)}
  ReverseDirection = false
  SafeHeight = 9.25217
  Side = 0
  SplitArcs = false
  StartDepth = 7
  StartPoint = (0,0,0)
  StepDown = 3
  ToolController = -> __4mm_Endmill
  UseComp = true
  UseStartPoint = false
  processCircles = false
  processHoles = false
  processPerimeter = true
  expr: ClearanceHeight = OpStockZMax + SetupSheet.ClearanceHeightOffset
  expr: FinalDepth = 0.2
  expr: SafeHeight = OpStockZMax + SetupSheet.SafeHeightOffset
  expr: StartDepth = <<Spreadsheet>>.Thickness
  expr: StepDown = 3
FEATURE [Part::FeaturePython] ToolBit003  label="3mm_Endmill"  # Path/CAM toolbit (typed FeaturePython)
  BitPropertyNames = Chipload | CuttingEdgeHeight | Diameter | Flutes | Length | Material | ShankDiameter
  BitShape = <path>
  Chipload = 0
  CuttingEdgeHeight = 10
  Diameter = 3
  File = <userpath>/MensShed/CNCRouter/FreeCAD/Bit/3mm_Endmill.fctb
  Flutes = 0
  Length = 50
  Material = 0
  ShankDiameter = 6.4
  ShapeName = endmill
FEATURE [Path::FeaturePython] _mm_Endmill  label="3mm_Endmill001"  # Path/CAM operation (typed FeaturePython)
  HorizFeed = 11.9333
  HorizRapid = 0
  SpindleDir = 0
  SpindleSpeed = 23873
  Tool = -> ToolBit003
  ToolNumber = 3
  VertFeed = 5.96667
  VertRapid = 0
  expr: HorizRapid = SetupSheet.HorizRapid
  expr: VertRapid = SetupSheet.VertRapid
FEATURE [App::DocumentObjectGroup] Tools
  Group = -> [__4mm_Endmill,_mm_Endmill]
FEATURE [Mesh::FeaturePython] CutMaterial  # WARN: FeaturePython — macro-defined, semantics opaque (R4)
FEATURE [App::FeaturePython] SetupSheet001  # Path/CAM operation (typed FeaturePython)
  ClearanceHeightExpression = OpStockZMax+SetupSheet001.ClearanceHeightOffset
  ClearanceHeightOffset = 5
  CoolantMode = 0
  CoolantModes = None | Flood | Mist
  FinalDepthExpression = OpFinalDepth
  HorizRapid = 0
  SafeHeightExpression = OpStockZMax+SetupSheet001.SafeHeightOffset
  SafeHeightOffset = 3
  StartDepthExpression = OpStartDepth
  StepDownExpression = OpToolDiameter
  VertRapid = 0
FEATURE [Part::FeaturePython] Clone005  label="Model-Body001"  # Draft clone (typed FeaturePython)
  AttacherType = Attacher::AttachEngine3D
  Fuse = false
  Objects = -> [Body]
  PathResource = Model
  Placement = pos=(-2,0,0) rot=(0,0,1;0rad)
  Scale = (1,1,1)
FEATURE [Part::FeaturePython] Clone006  label="Model-Body (mirrored) 001"  # Draft clone (typed FeaturePython)
  AttacherType = Attacher::AttachEngine3D
  Fuse = false
  Objects = -> [mirror]
  PathResource = Model
  Placement = pos=(-113.202,287.893,10.586) rot=(0.99989,0.002927,-0.014571;3.14394rad)
  Scale = (1,1,1)
FEATURE [Part::FeaturePython] Clone007  label="Model-BottomShelf001"  # Draft clone (typed FeaturePython)
  AttacherType = Attacher::AttachEngine3D
  Fuse = false
  Objects = -> [Body003]
  PathResource = Model
  Placement = pos=(1,-4,0) rot=(0,0,1;0rad)
  Scale = (1,1,1)
FEATURE [Part::FeaturePython] Clone008  label="Model-MidShelf001"  # Draft clone (typed FeaturePython)
  AttacherType = Attacher::AttachEngine3D
  Fuse = false
  Objects = -> [Body002]
  PathResource = Model
  Placement = pos=(7,6,0) rot=(0,0,1;0rad)
  Scale = (1,1,1)
FEATURE [Part::FeaturePython] Clone009  label="Model-TopShelf001"  # Draft clone (typed FeaturePython)
  AttacherType = Attacher::AttachEngine3D
  Fuse = false
  Objects = -> [Body001]
  PathResource = Model
  Placement = pos=(-7,-1,0) rot=(0,0,1;0rad)
  Scale = (1,1,1)
FEATURE [App::DocumentObjectGroup] Model001
  Group = -> [Clone005,Clone006,Clone007,Clone008,Clone009]
FEATURE [Part::FeaturePython] ToolBit005  label="3mm_Endmill002"  # Path/CAM toolbit (typed FeaturePython)
  BitPropertyNames = Chipload | CuttingEdgeHeight | Diameter | Flutes | Length | Material | ShankDiameter
  BitShape = <path>
  Chipload = 0
  CuttingEdgeHeight = 10
  Diameter = 3
  File = <userpath>/MensShed/CNCRouter/FreeCAD/Bit/3mm_Endmill.fctb
  Flutes = 0
  Length = 50
  Material = 0
  ShankDiameter = 6.4
  ShapeName = endmill
FEATURE [Path::FeaturePython] _mm_Endmill002  label="3mm_Endmill003"  # Path/CAM operation (typed FeaturePython)
  HorizFeed = 10
  HorizRapid = 0
  SpindleDir = 0
  SpindleSpeed = 15000
  Tool = -> ToolBit005
  ToolNumber = 2
  VertFeed = 20
  VertRapid = 0
  expr: HorizRapid = SetupSheet001.HorizRapid
  expr: VertRapid = SetupSheet001.VertRapid
FEATURE [App::DocumentObjectGroup] Tools001
  Group = -> [_mm_Endmill002]
FEATURE [Path::FeaturePython] Profile004  label="Slots001"  # Path/CAM operation (typed FeaturePython)
  Active = true
  AreaParams:
    Tolerance = 1e-07
    FitArcs = True
    Simplify = False
    CleanDistance = 0.0
    Accuracy = 0.01
    Unit = 1.0
    MinArcPoints = 4
    MaxArcPoints = 100
    ClipperScale = 10000000.0
    Fill = 0
    Coplanar = 0
    Reorient = True
    Outline = False
    Explode = False
    OpenMode = 0
    Deflection = 0.01
    SubjectFill = 0
    ClipFill = 0
    Offset = -1.5
    ExtraPass = 0
    Stepover = 0.0
    LastStepover = 0.0
    JoinType = 0
    EndType = 0
    MiterLimit = 2.0
    RoundPrecision = 0.0
    PocketMode = 0
    ToolRadius = 1.0
    PocketExtraOffset = 0.0
    PocketStepover = 0.0
    PocketLastStepover = 0.0
    FromCenter = False
    Angle = 45.0
    AngleShift = 0.0
    Shift = 0.0
    Thicken = False
    SectionCount = -1
    Stepdown = 1.0
    SectionOffset = 0.0
    SectionTolerance = 1e-06
    SectionMode = 2
    Project = False
  AttemptInverseAngle = true
  Base = -> [Clone]
  ClearanceHeight = 10.5022
  CoolantMode = 0
  CycleTime = 00:02:04
  Direction = 0
  EnableRotation = 0
  FinalDepth = 0.2
  HandleMultipleFeatures = 0
  InverseAngle = false
  JoinType = 0
  LimitDepthToFace = true
  MiterLimit = 0.1
  OffsetExtra = 0
  OpFinalDepth = 7
  OpStartDepth = 9
  OpStockZMax = 5.50217
  OpStockZMin = -1.66783
  OpToolDiameter = 3
  PathParams = {'orientation': 1, 'feedrate': 10.0, 'feedrate_v': 20.0, 'verbose': True, 'resume_height': 8.502171129369497, 'retraction': 10.502171129369497, 'return_end': True, 'preamble': False, 'start': Vector (34.499999849999995, 118.0, 10.502171129369497)}
  ReverseDirection = false
  SafeHeight = 8.50217
  Side = 1
  SplitArcs = false
  StartDepth = 7
  StartPoint = (0,0,0)
  StepDown = 2
  ToolController = -> _mm_Endmill002
  UseComp = true
  UseStartPoint = false
  processCircles = false
  processHoles = false
  processPerimeter = true
  expr: ClearanceHeight = OpStockZMax + SetupSheet001.ClearanceHeightOffset
  expr: FinalDepth = 0.2
  expr: SafeHeight = OpStockZMax + SetupSheet001.SafeHeightOffset
  expr: StartDepth = 7
  expr: StepDown = 2
FEATURE [Part::FeaturePython] Stock002  # WARN: FeaturePython — macro-defined, semantics opaque (R4)
  Height = 7.17
  Length = 538.57
  Placement = pos=(-2,-1,-1.66783) rot=(0,0,1;0rad)
  StockType = CreateBox
  Width = 291
FEATURE [Path::FeaturePython] Profile005  label="SlotsMirror"  # Path/CAM operation (typed FeaturePython)
  Active = true
  AreaParams:
    Tolerance = 1e-07
    FitArcs = True
    Simplify = False
    CleanDistance = 0.0
    Accuracy = 0.01
    Unit = 1.0
    MinArcPoints = 4
    MaxArcPoints = 100
    ClipperScale = 10000000.0
    Fill = 0
    Coplanar = 0
    Reorient = True
    Outline = False
    Explode = False
    OpenMode = 0
    Deflection = 0.01
    SubjectFill = 0
    ClipFill = 0
    Offset = -1.5
    ExtraPass = 0
    Stepover = 0.0
    LastStepover = 0.0
    JoinType = 0
    EndType = 0
    MiterLimit = 2.0
    RoundPrecision = 0.0
    PocketMode = 0
    ToolRadius = 1.0
    PocketExtraOffset = 0.0
    PocketStepover = 0.0
    PocketLastStepover = 0.0
    FromCenter = False
    Angle = 45.0
    AngleShift = 0.0
    Shift = 0.0
    Thicken = False
    SectionCount = -1
    Stepdown = 1.0
    SectionOffset = 0.0
    SectionTolerance = 1e-06
    SectionMode = 2
    Project = False
  AttemptInverseAngle = true
  Base = -> [Clone001]
  ClearanceHeight = 10.5022
  CoolantMode = 0
  CycleTime = 00:02:20
  Direction = 0
  EnableRotation = 0
  FinalDepth = 0.2
  HandleMultipleFeatures = 0
  InverseAngle = false
  JoinType = 0
  LimitDepthToFace = true
  MiterLimit = 0.1
  OffsetExtra = 0
  OpFinalDepth = 5.98416
  OpStartDepth = 6.05378
  OpStockZMax = 5.50217
  OpStockZMin = -1.66783
  OpToolDiameter = 3
  PathParams = {'orientation': 1, 'feedrate': 10.0, 'feedrate_v': 20.0, 'verbose': True, 'resume_height': 8.502171129369497, 'retraction': 10.502171129369497, 'return_end': True, 'preamble': False, 'start': Vector (104.88471221266929, 263.7828037142617, 10.502171129369497)}
  ReverseDirection = false
  SafeHeight = 8.50217
  Side = 1
  SplitArcs = false
  StartDepth = 7
  StartPoint = (0,0,0)
  StepDown = 2
  ToolController = -> _mm_Endmill002
  UseComp = true
  UseStartPoint = false
  processCircles = false
  processHoles = false
  processPerimeter = true
  expr: ClearanceHeight = OpStockZMax + SetupSheet001.ClearanceHeightOffset
  expr: FinalDepth = 0.2
  expr: SafeHeight = OpStockZMax + SetupSheet001.SafeHeightOffset
  expr: StartDepth = 7
  expr: StepDown = 2
FEATURE [Mesh::FeaturePython] CutMaterial002  # WARN: FeaturePython — macro-defined, semantics opaque (R4)
FEATURE [Path::FeaturePython] Array  label="SlotsArray"  # Path/CAM operation (typed FeaturePython)
  Active = true
  Angle = 0
  Base = -> Profile004
  Centre = (0,0,0)
  Copies = 0
  CopiesX = 1
  CopiesY = 2
  JitterSeed = 0
  Offset = (550,300,0)
  ToolController = -> _mm_Endmill002
  Type = 1
FEATURE [App::MeasureDistance] Distance  label="Distance: 538.64 mm"
  Distance = 538.639
  P1 = (-2,272.054,7)
  P2 = (536.567,263.267,7)
FEATURE [Path::FeaturePython] Array001  label="MirrorArray"  # Path/CAM operation (typed FeaturePython)
  Active = true
  Angle = 0
  Base = -> Profile005
  Centre = (0,0,0)
  Copies = 0
  CopiesX = 1
  CopiesY = 2
  JitterSeed = 0
  Offset = (550,300,0)
  ToolController = -> _mm_Endmill002
  Type = 1
FEATURE [Path::FeatureCompoundPython] Operations001  label="Operations3mm"  # Path/CAM operation (typed FeaturePython)
  Group = -> [Profile004,Profile005,Array,Array001]
  UsePlacements = false
FEATURE [Path::FeaturePython] Job001  label="Job3mmBit"  # Path/CAM operation (typed FeaturePython)
  CycleTime = 00:08:48
  Fixtures = G54
  GeometryTolerance = 0.01
  JobType = 0
  LastPostProcessDate = 2022-05-25 08:39:39.845903
  LastPostProcessOutput = <userpath>/MensShed/CNCRouter/Shapes/Stand5_DB-3mm.ngc
  Model = -> Model001
  Operations = -> Operations001
  OrderOutputBy = 0
  PostProcessor = 2
  PostProcessorOutputFile = %D/%d-3mm.ngc
  SetupSheet = -> SetupSheet001
  SplitOutput = false
  Stock = -> Stock002
  Tools = -> Tools001
FEATURE [Path::FeaturePython] Array002  label="BaseInnerArray"  # Path/CAM operation (typed FeaturePython)
  Active = true
  Angle = 0
  Base = -> Profile
  Centre = (0,0,0)
  Copies = 0
  CopiesX = 1
  CopiesY = 2
  JitterSeed = 0
  Offset = (550,300,0)
  ToolController = -> __4mm_Endmill
  Type = 1
FEATURE [Path::FeaturePython] Array003  label="MirrorInnerArray"  # Path/CAM operation (typed FeaturePython)
  Active = true
  Angle = 0
  Base = -> Profile001
  Centre = (0,0,0)
  Copies = 0
  CopiesX = 1
  CopiesY = 2
  JitterSeed = 0
  Offset = (550,300,0)
  ToolController = -> __4mm_Endmill
  Type = 1
FEATURE [Path::FeaturePython] Array004  label="ProfileArray"  # Path/CAM operation (typed FeaturePython)
  Active = true
  Angle = 0
  Base = -> Profile002
  Centre = (0,0,0)
  Copies = 0
  CopiesX = 1
  CopiesY = 2
  JitterSeed = 0
  Offset = (550,300,0)
  ToolController = -> __4mm_Endmill
  Type = 1
FEATURE [Path::FeatureCompoundPython] Operations  label="Operations6mm"  # Path/CAM operation (typed FeaturePython)
  Group = -> [Profile,Profile001,Profile002,Array002,Array003,Array004]
  UsePlacements = false
FEATURE [Path::FeaturePython] Job  label="Job6mmBit"  # Path/CAM operation (typed FeaturePython)
  CycleTime = 00:43:14
  Fixtures = G54
  GeometryTolerance = 0.01
  JobType = 0
  LastPostProcessDate = 2022-05-25 08:39:44.412093
  LastPostProcessOutput = <userpath>/MensShed/CNCRouter/Shapes/Stand5_DB-6mmBit.ngc
  Model = -> Model
  Operations = -> Operations
  OrderOutputBy = 0
  PostProcessor = 2
  PostProcessorOutputFile = %D/%d-6mmBit.ngc
  SetupSheet = -> SetupSheet
  SplitOutput = false
  Stock = -> Stock001
  Tools = -> Tools
FEATURE [App::MeasureDistance] Distance001  label="Distance: 1094.97 mm"
  Distance = 1094.97
  P1 = (-5.19804,759.543,4)
  P2 = (1089.77,758.235,4)
FEATURE [App::MeasureDistance] Distance002  label="Distance: 893.21 mm"
  Distance = 893.206
  P1 = (505.645,0,7)
  P2 = (504.337,893.2,4)
note: 5 file-system paths scrubbed to <path> (originals preserved in the JSON sidecar)
